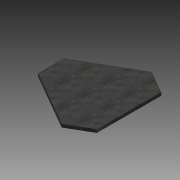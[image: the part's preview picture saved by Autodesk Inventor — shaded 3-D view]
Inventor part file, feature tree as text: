
AUTODESK INVENTOR PART (.ipt)
format: ipt  version: 2015 (Build 190159000, 159)  size: 83,968 bytes
history: native  units: in
note: dims shown in document units (in); Inventor stores cm internally (conversion verified against a paired STEP export)
features: extrude x1, sketch x1
ambient origin geometry x8: Origin, YZ Plane, XZ Plane, XY Plane, X Axis, Y Axis, Z Axis, Center Point
bodies: Solid1 (feature_tree)
feature tree (2):
  extrude  "Extrusion1"  Depth=1.0in
  sketch  "Sketch1"  dims[d0=8.0in d6=20.0in d21=1.0in d22=0.0in]
